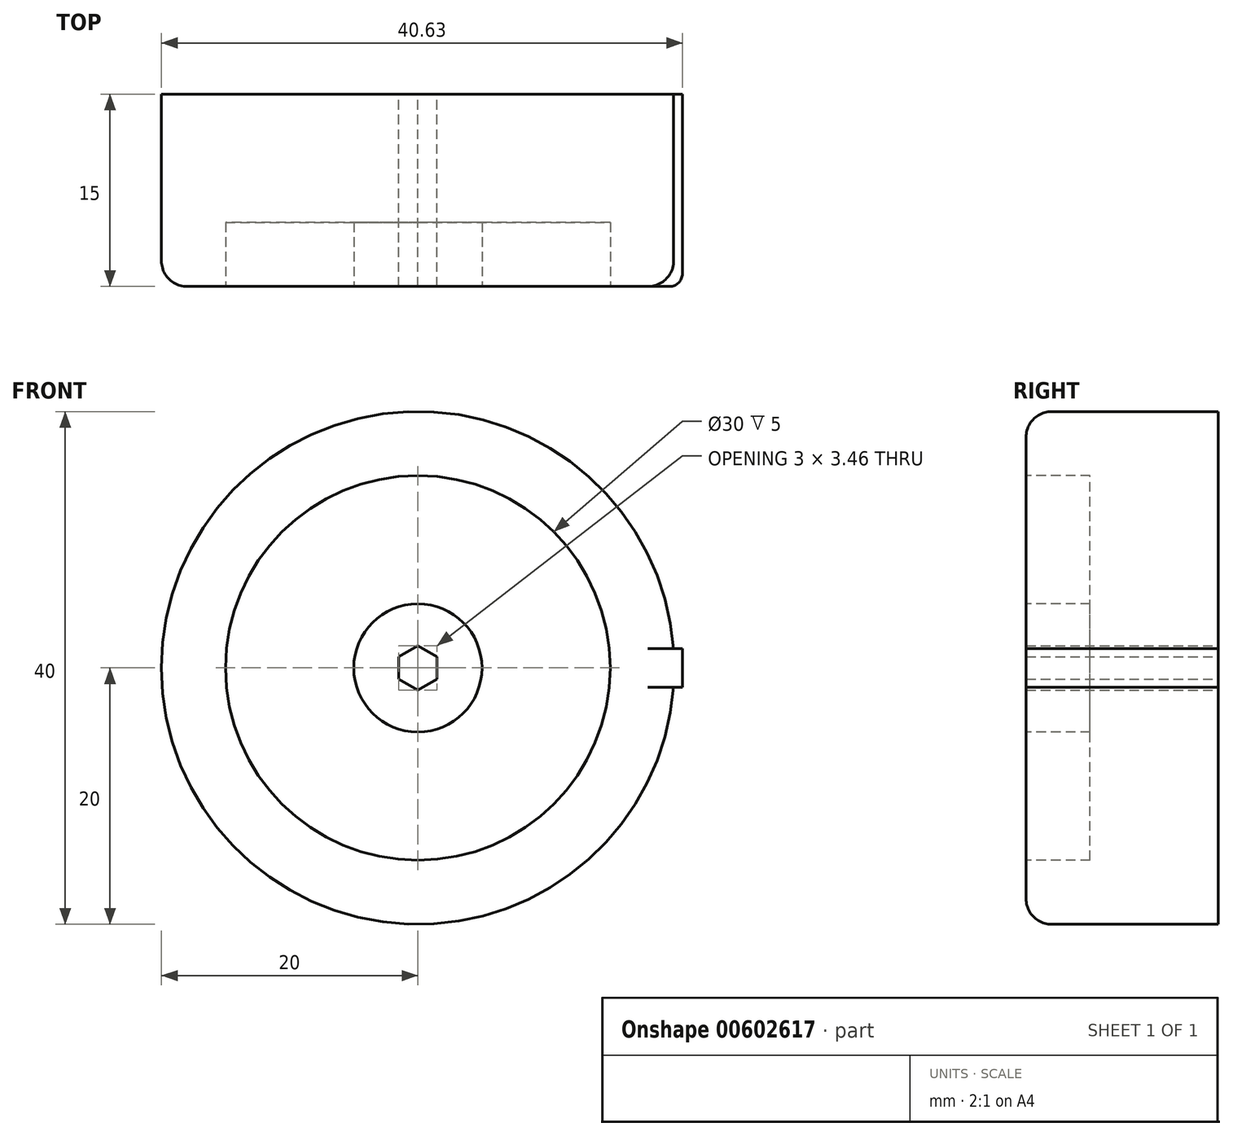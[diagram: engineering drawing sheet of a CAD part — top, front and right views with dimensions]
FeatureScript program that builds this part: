
annotation { "Feature Type Name" : "Feature", "Feature Type Description" : "" }
export const myFeature = defineFeature(function(context is Context, id is Id, definition is map)
    precondition{}
    {
        {
            var Q0;
            Q0=qCreatedBy(makeId("Front.planeOp"),FACE);
            var sketch = newSketch(context, id + "F0", { "sketchPlane" : qUnion([Q0])});
            skCircle(sketch, "E0", {"center": v(0, 0) * mm, "radius": 20 * mm});
            skLineSegment(sketch, "E1.bottom", {"start": v(20.63, 1.5) * mm, "end": v(19.37, 1.5) * mm});
            skLineSegment(sketch, "E1.top", {"start": v(20.63, -1.5) * mm, "end": v(19.37, -1.5) * mm});
            skLineSegment(sketch, "E1.left", {"start": v(20.63, 1.5) * mm, "end": v(20.63, -1.5) * mm});
            skLineSegment(sketch, "E1.right", {"start": v(19.37, 1.5) * mm, "end": v(19.37, -1.5) * mm});
            skPoint(sketch, "E1.middle", {"position": v(20, 0) * mm});
            skLineSegment(sketch, "E2.anchor1", {"start": v(0, 0) * mm, "end": v(19.37, 1.5) * mm, "construction": true});
            skLineSegment(sketch, "E2.anchor2", {"start": v(0, 0) * mm, "end": v(19.37, 1.5) * mm, "construction": true});
            skSolve(sketch);
        }
        {
            var Q0;
            Q0 = qSketchRegion(id + "F0", true);
            extrude(context, id + "F1", {"entities" : qUnion([Q0]), "depth" : 15 * mm, "offsetDistance" : 25 * mm});
        }
        {
            var Q0;
            Q0=makeQuery(id+"F1.opExtrude","CAP_EDGE",EDGE,{"disambiguationData":[OSD([sQuery(id+"F0.wireOp",EDGE,"E0")])],"isStart":false});
            fillet(context, id + "F2", {"entities" : qUnion([Q0]), "radius" : 2 * mm, "tangentPropagation" : true, "allowEdgeOverflow" : false});
        }
        {
            var Q0;
            Q0=makeQuery(id+"F1.opExtrude","CAP_FACE",FACE,{"disambiguationData":[OSD([sQuery(id+"F0.wireOp",EDGE,"E0"),sQuery(id+"F0.wireOp",EDGE,"2a95798e-29ce-4d5e-8363-e2cf66f4b9d0.0"),sQuery(id+"F0.wireOp",EDGE,"2a95798e-29ce-4d5e-8363-e2cf66f4b9d0.1"),sQuery(id+"F0.wireOp",EDGE,"2a95798e-29ce-4d5e-8363-e2cf66f4b9d0.2"),sQuery(id+"F0.wireOp",EDGE,"2a95798e-29ce-4d5e-8363-e2cf66f4b9d0.3"),sQuery(id+"F0.wireOp",EDGE,"2a95798e-29ce-4d5e-8363-e2cf66f4b9d0.4"),sQuery(id+"F0.wireOp",EDGE,"2a95798e-29ce-4d5e-8363-e2cf66f4b9d0.5")])],"isStart":false});
            var sketch = newSketch(context, id + "F3", { "sketchPlane" : qUnion([Q0])});
            skCircle(sketch, "E3", {"center": v(0, 0) * mm, "radius": 15 * mm});
            skCircle(sketch, "E4", {"center": v(0, 0) * mm, "radius": 5 * mm});
            skSolve(sketch);
        }
        {
            var Q0;
            Q0=makeQuery(id+"F3.imprint","IMPRINT",FACE,{"disambiguationData":[TD([[makeQuery(id+"F3.imprint","IMPRINT",EDGE,{"derivedFrom":sQuery(id+"F3.wireOp",EDGE,"E3")}),1.0]])]});
            extrude(context, id + "F4", {"entities" : qUnion([Q0]), "operationType" : NewBodyOperationType.REMOVE, "oppositeDirection" : true, "depth" : 5 * mm, "offsetDistance" : 25 * mm});
        }
        {
            var Q0;
            Q0=qCreatedBy(makeId("Top.planeOp"),FACE);
            var sketch = newSketch(context, id + "F5", { "sketchPlane" : qUnion([Q0])});
            skLineSegment(sketch, "E5", {"start": v(0, 39.74) * mm, "end": v(0, -23.23) * mm});
            skSolve(sketch);
        }
        {
            var Q0;
            Q0=makeQuery(id+"F1.opExtrude","CAP_EDGE",EDGE,{"disambiguationData":[OSD([sQuery(id+"F0.wireOp",EDGE,"E1.left")])],"isStart":false});
            fillet(context, id + "F6", {"entities" : qUnion([Q0]), "radius" : 1 * mm, "tangentPropagation" : true, "allowEdgeOverflow" : false});
        }
        {
            var Q0;
            {var subQ5=sQuery(id+"F0.wireOp",EDGE,"E1.right");Q0=makeQuery(id+"F0.imprint","IMPRINT",FACE,{"disambiguationData":[TD([[makeQuery(id+"F0.imprint","IMPRINT",EDGE,{"derivedFrom":subQ5}),-1.0]])]});}
            var sketch = newSketch(context, id + "F7", { "sketchPlane" : qUnion([Q0])});
            skCircle(sketch, "E6.cCircle", {"center": v(0, 0) * mm, "radius": 1.5 * mm, "construction": true});
            skLineSegment(sketch, "E6.0", {"start": v(1.5, 0.87) * mm, "end": v(1.5, -0.87) * mm});
            skLineSegment(sketch, "E6.1", {"start": v(1.5, -0.87) * mm, "end": v(0, -1.73) * mm});
            skLineSegment(sketch, "E6.2", {"start": v(0, -1.73) * mm, "end": v(-1.5, -0.87) * mm});
            skLineSegment(sketch, "E6.3", {"start": v(-1.5, -0.87) * mm, "end": v(-1.5, 0.87) * mm});
            skLineSegment(sketch, "E6.4", {"start": v(-1.5, 0.87) * mm, "end": v(0, 1.73) * mm});
            skLineSegment(sketch, "E6.5", {"start": v(0, 1.73) * mm, "end": v(1.5, 0.87) * mm});
            skPoint(sketch, "E6.0.midPoint", {"position": v(1.5, 0) * mm});
            skSolve(sketch);
        }
        {
            var Q0;
            Q0 = qSketchRegion(id + "F7", true);
            extrude(context, id + "F8", {"entities" : qUnion([Q0]), "operationType" : NewBodyOperationType.REMOVE, "oppositeDirection" : true, "depth" : -25 * mm, "offsetDistance" : 25 * mm});
        }
    });
